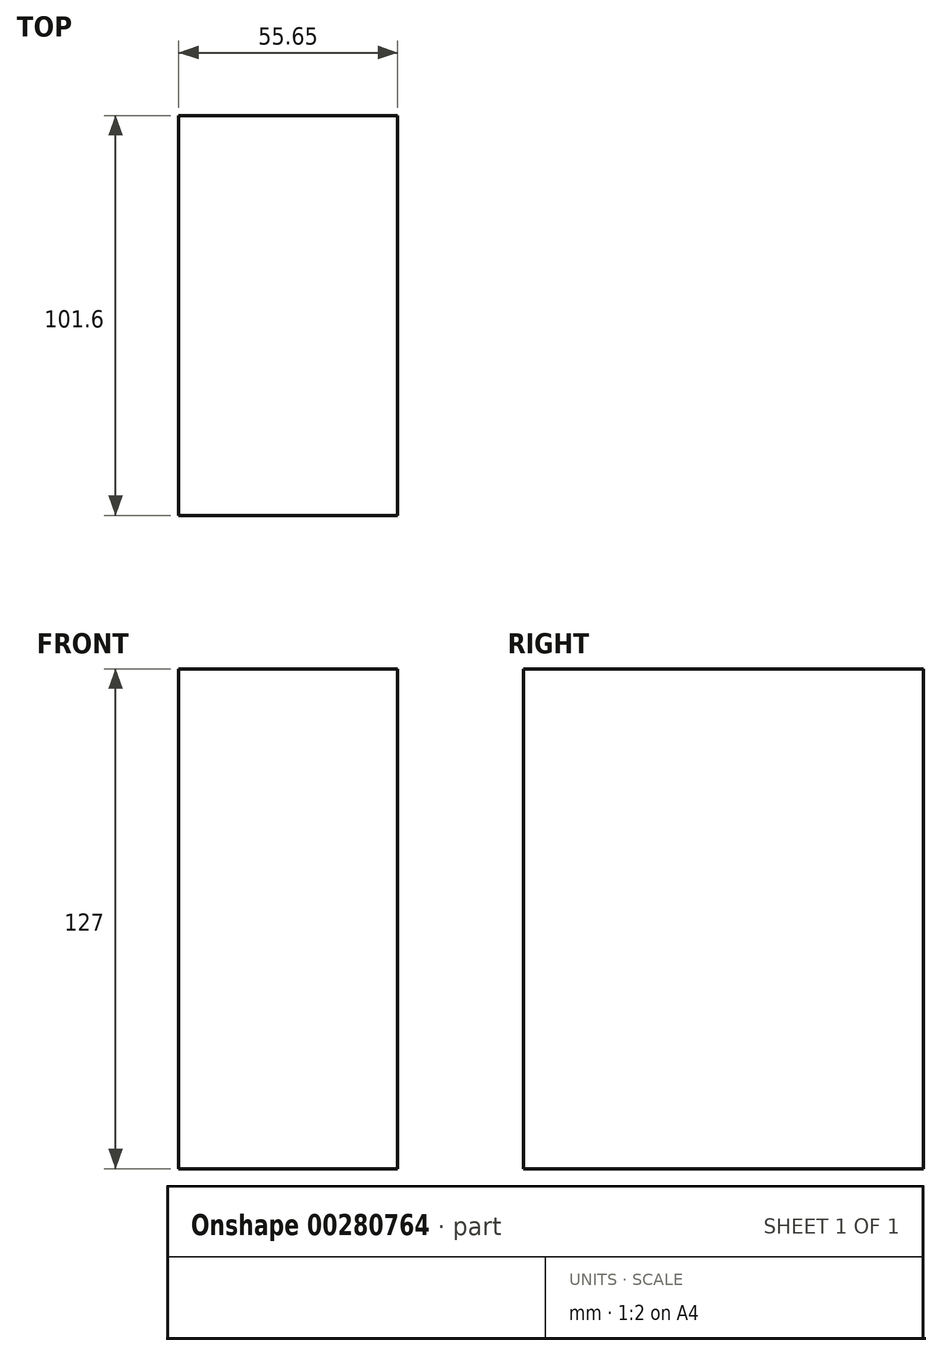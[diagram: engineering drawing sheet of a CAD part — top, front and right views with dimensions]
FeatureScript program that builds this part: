
annotation { "Feature Type Name" : "Feature", "Feature Type Description" : "" }
export const myFeature = defineFeature(function(context is Context, id is Id, definition is map)
    precondition{}
    {
        {
            var Q0;
            Q0=qCreatedBy(makeId("Top.planeOp"),FACE);
            var sketch = newSketch(context, id + "F0", { "sketchPlane" : qUnion([Q0])});
            skLineSegment(sketch, "E0.bottom", {"start": v(-53.61, 32.94) * mm, "end": v(-7.9, 32.94) * mm});
            skLineSegment(sketch, "E0.top", {"start": v(-53.61, -68.66) * mm, "end": v(-7.9, -68.66) * mm});
            skLineSegment(sketch, "E0.left", {"start": v(-53.61, 32.94) * mm, "end": v(-53.61, -68.66) * mm});
            skLineSegment(sketch, "E0.right", {"start": v(-7.9, 53.26) * mm, "end": v(-7.9, -68.66) * mm});
            skLineSegment(sketch, "E1.bottom", {"start": v(-7.9, -68.66) * mm, "end": v(2.04, -68.66) * mm});
            skLineSegment(sketch, "E1.top", {"start": v(-7.9, 32.94) * mm, "end": v(2.04, 32.94) * mm});
            skLineSegment(sketch, "E1.left", {"start": v(-7.9, -68.66) * mm, "end": v(-7.9, 32.94) * mm});
            skLineSegment(sketch, "E1.right", {"start": v(2.04, -68.66) * mm, "end": v(2.04, 32.94) * mm});
            skSolve(sketch);
        }
        {
            var Q0;
            Q0=makeQuery(id+"F0.imprint","IMPRINT",FACE,{"disambiguationData":[TD([[makeQuery(id+"F0.imprint","IMPRINT",EDGE,{"derivedFrom":sQuery(id+"F0.wireOp",EDGE,"E1.bottom")}),1.0]])]});
            var Q1;
            Q1=makeQuery(id+"F0.imprint","IMPRINT",FACE,{"disambiguationData":[TD([[makeQuery(id+"F0.imprint","IMPRINT",EDGE,{"derivedFrom":sQuery(id+"F0.wireOp",EDGE,"E0.bottom")}),-1.0]])]});
            extrude(context, id + "F1", {"entities" : qUnion([Q0, Q1]), "depth" : 127 * mm});
        }
    });
